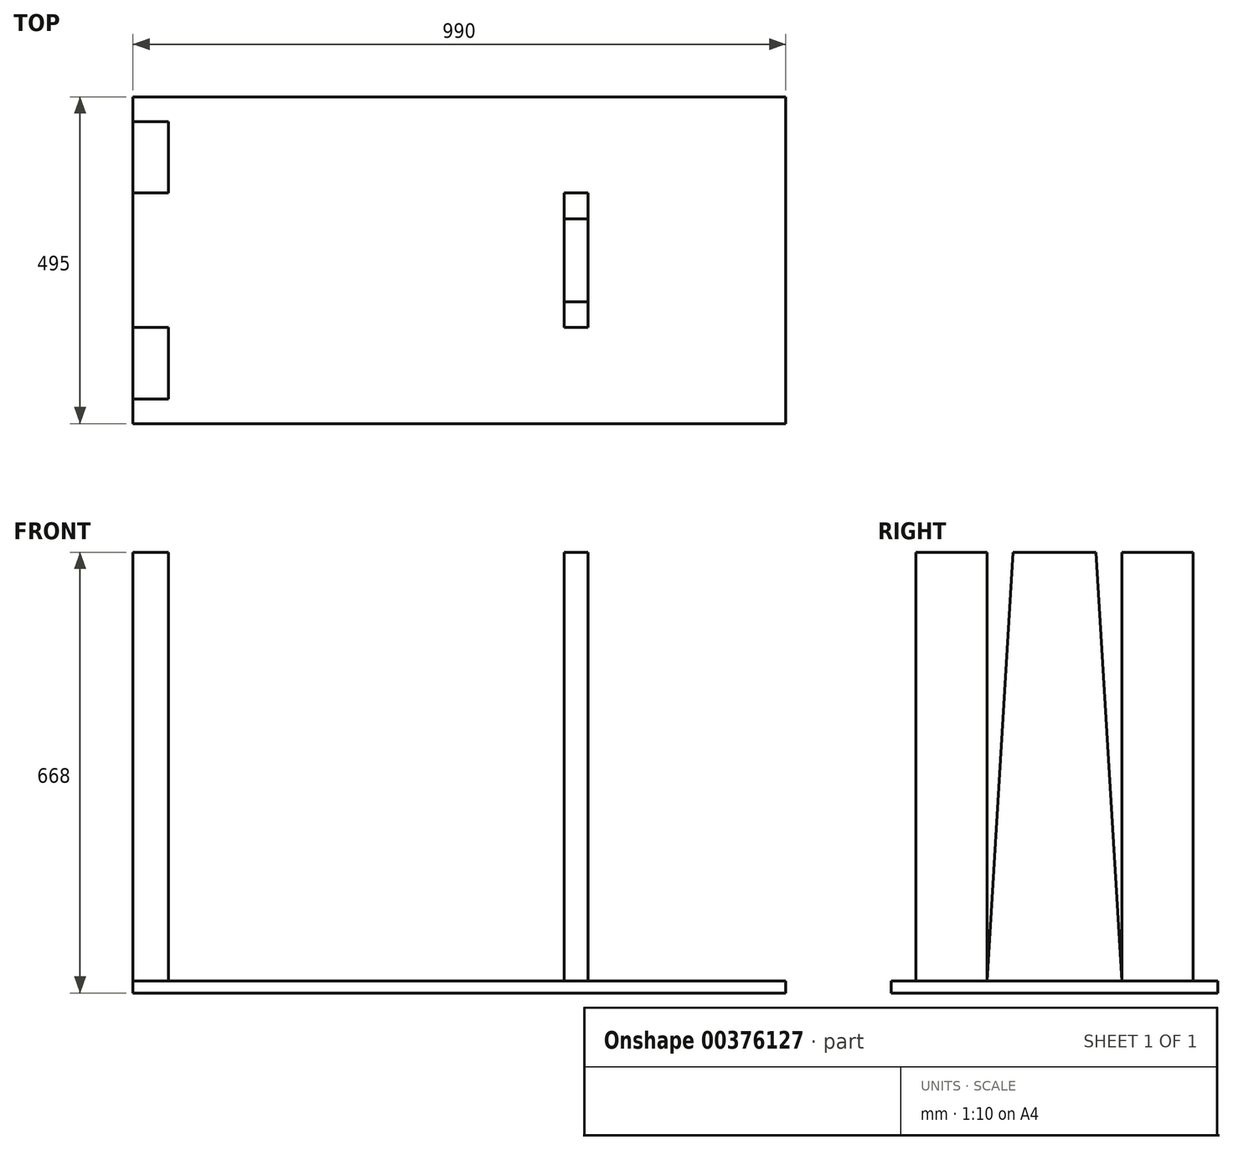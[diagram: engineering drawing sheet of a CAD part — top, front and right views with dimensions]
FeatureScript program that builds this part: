
annotation { "Feature Type Name" : "Feature", "Feature Type Description" : "" }
export const myFeature = defineFeature(function(context is Context, id is Id, definition is map)
    precondition{}
    {
        {
            var Q0;
            Q0=qCreatedBy(makeId("Top.planeOp"),FACE);
            var sketch = newSketch(context, id + "F0", { "sketchPlane" : qUnion([Q0])});
            skLineSegment(sketch, "E0.bottom", {"start": v(-495, 247.5) * mm, "end": v(495, 247.5) * mm});
            skLineSegment(sketch, "E0.top", {"start": v(-495, -247.5) * mm, "end": v(495, -247.5) * mm});
            skLineSegment(sketch, "E0.left", {"start": v(-495, 247.5) * mm, "end": v(-495, -247.5) * mm});
            skLineSegment(sketch, "E0.right", {"start": v(495, 247.5) * mm, "end": v(495, -247.5) * mm});
            skPoint(sketch, "E1", {"position": v(0, 247.5) * mm});
            skPoint(sketch, "E2", {"position": v(-495, 0) * mm});
            skSolve(sketch);
        }
        {
            var Q0;
            Q0=qSketchRegion(id+"F0",true);
            extrude(context, id + "F1", {"entities" : qUnion([Q0]), "depth" : 18 * mm});
        }
        {
            var Q0;
            Q0=makeQuery(id+"F1.opExtrude","CAP_FACE",FACE,{"disambiguationData":[OSD([sQuery(id+"F0.wireOp",EDGE,"E0.bottom"),sQuery(id+"F0.wireOp",EDGE,"E0.top"),sQuery(id+"F0.wireOp",EDGE,"E0.left"),sQuery(id+"F0.wireOp",EDGE,"E0.right")])],"isStart":false});
            var sketch = newSketch(context, id + "F2", { "sketchPlane" : qUnion([Q0])});
            skPoint(sketch, "E3", {"position": v(-495, 0) * mm});
            skLineSegment(sketch, "E4.bottom", {"start": v(-495, 210) * mm, "end": v(-441, 210) * mm});
            skLineSegment(sketch, "E4.top", {"start": v(-495, -210) * mm, "end": v(-441, -210) * mm});
            skLineSegment(sketch, "E4.left", {"start": v(-495, 210) * mm, "end": v(-495, -210) * mm});
            skLineSegment(sketch, "E4.right", {"start": v(-441, 210) * mm, "end": v(-441, -210) * mm});
            skLineSegment(sketch, "E5.bottom", {"start": v(195, -102) * mm, "end": v(159, -102) * mm});
            skLineSegment(sketch, "E5.top", {"start": v(195, 102) * mm, "end": v(159, 102) * mm});
            skLineSegment(sketch, "E5.left", {"start": v(195, -102) * mm, "end": v(195, 102) * mm});
            skLineSegment(sketch, "E5.right", {"start": v(159, -102) * mm, "end": v(159, 102) * mm});
            skPoint(sketch, "E6", {"position": v(195, 0) * mm});
            skPoint(sketch, "E7", {"position": v(0, -247.5) * mm});
            skSolve(sketch);
        }
        {
            var Q0;
            {var subQ1=sQuery(id+"F2.wireOp",EDGE,"E4.bottom");Q0=makeQuery(id+"F2.imprint","IMPRINT",FACE,{"disambiguationData":[TD([[makeQuery(id+"F2.imprint","IMPRINT",EDGE,{"derivedFrom":subQ1}),-1.0]])]});}
            var Q1;
            Q1=makeQuery(id+"F2.imprint","IMPRINT",FACE,{"disambiguationData":[TD([[makeQuery(id+"F2.imprint","IMPRINT",EDGE,{"derivedFrom":sQuery(id+"F2.wireOp",EDGE,"1kVaZgk3-8Nhi-dGg9-Ba8R-nr3TmBuge7lK.bottom")}),-1.0]])]});
            var Q2;
            Q2=makeQuery(id+"F2.imprint","IMPRINT",FACE,{"disambiguationData":[TD([[makeQuery(id+"F2.imprint","IMPRINT",EDGE,{"derivedFrom":sQuery(id+"F2.wireOp",EDGE,"d1aede41-c4be-4dbf-9319-fc5a6116a92b.bottom")}),-1.0]])]});
            var Q3;
            {var subQ1=sQuery(id+"F2.wireOp",EDGE,"E5.bottom");Q3=makeQuery(id+"F2.imprint","IMPRINT",FACE,{"disambiguationData":[TD([[makeQuery(id+"F2.imprint","IMPRINT",EDGE,{"derivedFrom":subQ1}),-1.0]])]});}
            extrude(context, id + "F3", {"entities" : qUnion([Q0, Q1, Q2, Q3]), "depth" : 650 * mm});
        }
        {
            var Q0;
            Q0=makeQuery(id+"F3.opExtrude","SWEPT_FACE",FACE,{"disambiguationData":[OSD([sQuery(id+"F2.wireOp",EDGE,"E5.left")])]});
            var sketch = newSketch(context, id + "F4", { "sketchPlane" : qUnion([Q0])});
            skLineSegment(sketch, "E8.bottom", {"start": v(102, 18) * mm, "end": v(-102, 18) * mm});
            skLineSegment(sketch, "E8.top", {"start": v(102, 668) * mm, "end": v(-102, 668) * mm});
            skLineSegment(sketch, "E8.left", {"start": v(102, 18) * mm, "end": v(102, 668) * mm});
            skLineSegment(sketch, "E8.right", {"start": v(-102, 18) * mm, "end": v(-102, 668) * mm});
            skPoint(sketch, "E9", {"position": v(0, 18) * mm});
            skPoint(sketch, "E10", {"position": v(140, 18) * mm});
            skPoint(sketch, "E11", {"position": v(-140, 18) * mm});
            skPoint(sketch, "E12", {"position": v(140, 668) * mm});
            skPoint(sketch, "E13", {"position": v(-140, 668) * mm});
            skLineSegment(sketch, "E14", {"start": v(102, 18) * mm, "end": v(140, 668) * mm});
            skLineSegment(sketch, "E15", {"start": v(-140, 668) * mm, "end": v(-102, 18) * mm});
            skSolve(sketch);
        }
        {
            var Q0;
            {var subQ0=sQuery(id+"F4.wireOp",EDGE,"E8.left");Q0=makeQuery(id+"F4.imprint","IMPRINT",FACE,{"disambiguationData":[TD([[makeQuery(id+"F4.imprint","IMPRINT",EDGE,{"derivedFrom":subQ0}),-1.0]])]});}
            var Q1;
            {var subQ0=sQuery(id+"F4.wireOp",EDGE,"E8.right");Q1=makeQuery(id+"F4.imprint","IMPRINT",FACE,{"disambiguationData":[TD([[makeQuery(id+"F4.imprint","IMPRINT",EDGE,{"derivedFrom":subQ0}),1.0]])]});}
            var Q2;
            {var subQ3=sQuery(id+"F4.wireOp",EDGE,"ERWEisdO-8PsZ-Fccj-wROh-Rmm69zbihmoK");Q2=makeQuery(id+"F4.imprint","IMPRINT",FACE,{"disambiguationData":[TD([[makeQuery(id+"F4.imprint","IMPRINT",EDGE,{"derivedFrom":subQ3}),-1.0]])]});}
            var Q3;
            {var subQ3=sQuery(id+"F4.wireOp",EDGE,"njEO2kw1-x9P7-cku3-6qRM-CGIWQrq0eT6F");Q3=makeQuery(id+"F4.imprint","IMPRINT",FACE,{"disambiguationData":[TD([[makeQuery(id+"F4.imprint","IMPRINT",EDGE,{"derivedFrom":subQ3}),1.0]])]});}
            var Q4;
            {var subQ0=sQuery(id+"F4.wireOp",EDGE,"ERWEisdO-8PsZ-Fccj-wROh-Rmm69zbihmoK");Q4=makeQuery(id+"F4.imprint","IMPRINT",FACE,{"disambiguationData":[TD([[makeQuery(id+"F4.imprint","IMPRINT",EDGE,{"derivedFrom":subQ0}),1.0]])]});}
            var Q5;
            {var subQ0=sQuery(id+"F4.wireOp",EDGE,"njEO2kw1-x9P7-cku3-6qRM-CGIWQrq0eT6F");Q5=makeQuery(id+"F4.imprint","IMPRINT",FACE,{"disambiguationData":[TD([[makeQuery(id+"F4.imprint","IMPRINT",EDGE,{"derivedFrom":subQ0}),-1.0]])]});}
            extrude(context, id + "F5", {"entities" : qUnion([Q0, Q1, Q2, Q3, Q4, Q5]), "operationType" : NewBodyOperationType.REMOVE, "endBound" : BoundingType.THROUGH_ALL, "oppositeDirection" : true, "depth" : 25 * mm});
        }
        {
            var Q0;
            Q0=makeQuery(id+"F3.opExtrude","SWEPT_FACE",FACE,{"disambiguationData":[OSD([sQuery(id+"F2.wireOp",EDGE,"E4.left")])]});
            var sketch = newSketch(context, id + "F6", { "sketchPlane" : qUnion([Q0])});
            skLineSegment(sketch, "E16.bottom", {"start": v(210, 18) * mm, "end": v(-210, 18) * mm});
            skLineSegment(sketch, "E16.top", {"start": v(210, 668) * mm, "end": v(-210, 668) * mm});
            skLineSegment(sketch, "E16.left", {"start": v(210, 18) * mm, "end": v(210, 668) * mm});
            skLineSegment(sketch, "E16.right", {"start": v(-210, 18) * mm, "end": v(-210, 668) * mm});
            skPoint(sketch, "E17", {"position": v(0, 18) * mm});
            skPoint(sketch, "E18", {"position": v(140, 18) * mm});
            skPoint(sketch, "E19", {"position": v(-140, 18) * mm});
            skLineSegment(sketch, "E20", {"start": v(180.15, 668) * mm, "end": v(-180.15, 668) * mm});
            skPoint(sketch, "E21", {"position": v(140, 668) * mm});
            skPoint(sketch, "E22", {"position": v(-140, 668) * mm});
            skLineSegment(sketch, "E23", {"start": v(210, 18) * mm, "end": v(140, 668) * mm});
            skLineSegment(sketch, "E24", {"start": v(-140, 668) * mm, "end": v(-210, 18) * mm});
            skSolve(sketch);
        }
        {
            var Q0;
            {var subQ1=sQuery(id+"F2.wireOp",EDGE,"E5.bottom");Q0=makeQuery(id+"F2.imprint","IMPRINT",FACE,{"disambiguationData":[TD([[makeQuery(id+"F2.imprint","IMPRINT",EDGE,{"derivedFrom":subQ1}),-1.0]])]});}
            extrude(context, id + "F7", {"entities" : qUnion([Q0]), "depth" : 650 * mm});
        }
        {
            var Q0;
            Q0=makeQuery(id+"F7.opExtrude","SWEPT_FACE",FACE,{"disambiguationData":[OSD([sQuery(id+"F2.wireOp",EDGE,"E5.left")])]});
            var sketch = newSketch(context, id + "F8", { "sketchPlane" : qUnion([Q0])});
            skLineSegment(sketch, "E25", {"start": v(63, 668) * mm, "end": v(-63, 668) * mm});
            skPoint(sketch, "E26", {"position": v(0, 668) * mm});
            skLineSegment(sketch, "E27", {"start": v(-102, 18) * mm, "end": v(-63, 668) * mm});
            skLineSegment(sketch, "E28", {"start": v(102, 18) * mm, "end": v(63, 668) * mm});
            skSolve(sketch);
        }
        {
            var Q0;
            {var subQ0=sQuery(id+"F8.wireOp",EDGE,"E28");Q0=makeQuery(id+"F8.imprint","IMPRINT",FACE,{"disambiguationData":[TD([[makeQuery(id+"F8.imprint","IMPRINT",EDGE,{"derivedFrom":subQ0}),-1.0]])]});}
            var Q1;
            {var subQ0=sQuery(id+"F8.wireOp",EDGE,"E27");Q1=makeQuery(id+"F8.imprint","IMPRINT",FACE,{"disambiguationData":[TD([[makeQuery(id+"F8.imprint","IMPRINT",EDGE,{"derivedFrom":subQ0}),1.0]])]});}
            extrude(context, id + "F9", {"entities" : qUnion([Q0, Q1]), "operationType" : NewBodyOperationType.REMOVE, "oppositeDirection" : true, "depth" : 40 * mm});
        }
    });
